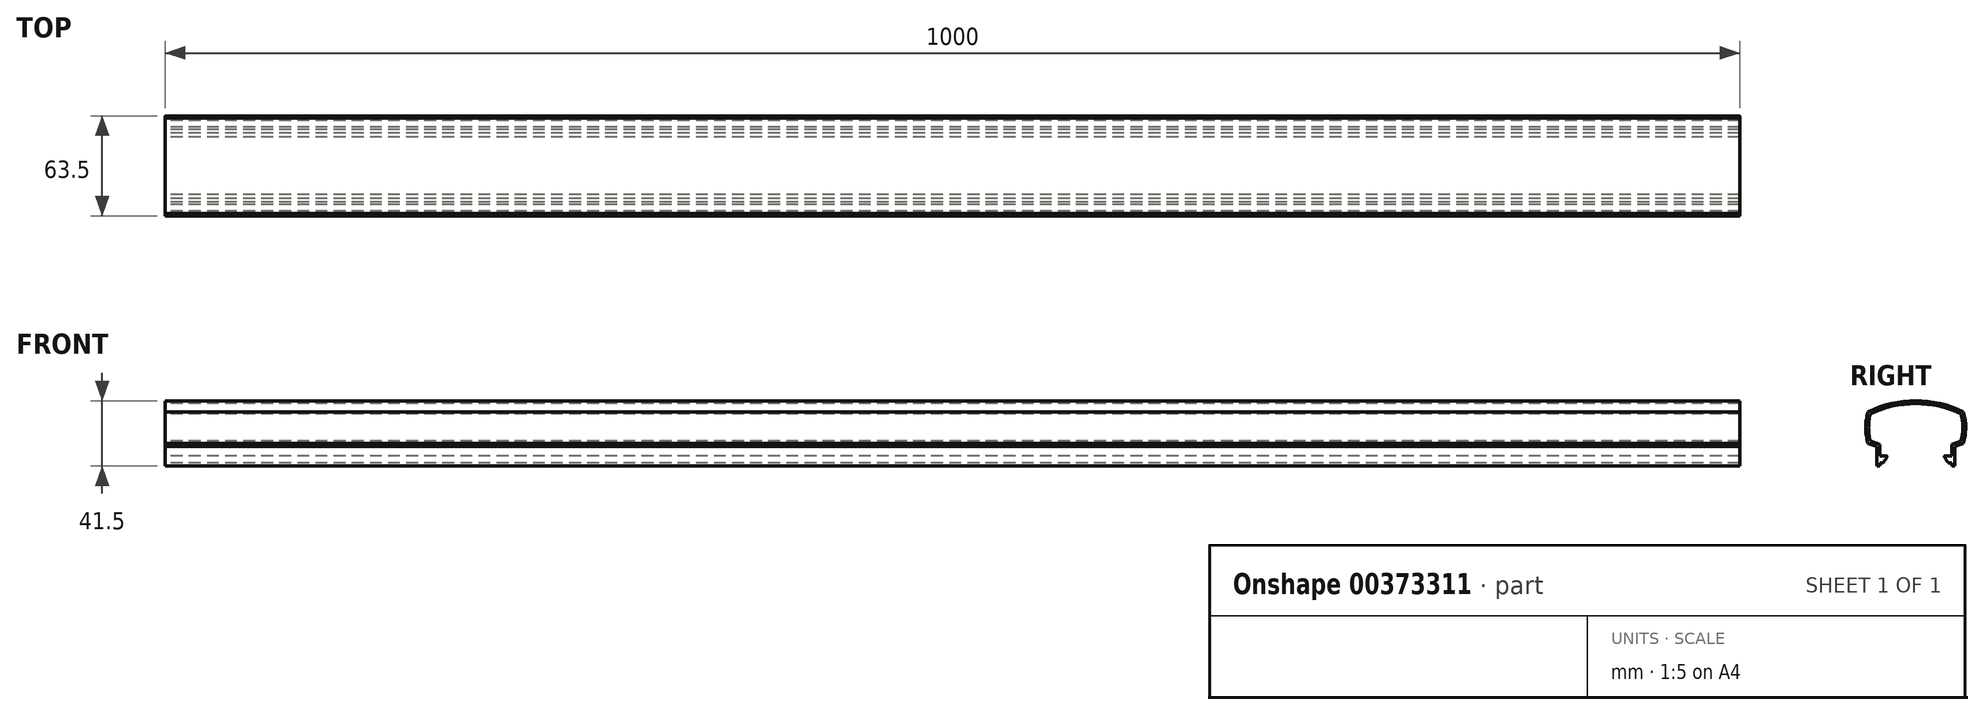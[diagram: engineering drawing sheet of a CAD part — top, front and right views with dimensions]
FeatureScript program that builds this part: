
annotation { "Feature Type Name" : "Feature", "Feature Type Description" : "" }
export const myFeature = defineFeature(function(context is Context, id is Id, definition is map)
    precondition{}
    {
        {
            var Q0;
            Q0=qCreatedBy(makeId("Right.planeOp"),FACE);
            var sketch = newSketch(context, id + "F0", { "sketchPlane" : qUnion([Q0])});
            skLineSegment(sketch, "E0.MirrorCS", {"start": v(56.45, 12.5) * mm, "end": v(56.45, 0) * mm});
            skLineSegment(sketch, "E1.MirrorCS", {"start": v(7.05, 12.5) * mm, "end": v(7.05, 0) * mm});
            skLineSegment(sketch, "E2", {"start": v(56.45, 12.5) * mm, "end": v(62.05, 14.54) * mm});
            skArc(sketch, "E3.trimOffspring", {"start": v(62.05, 14.54) * mm, "mid": v(63.5, 24.45) * mm, "end": v(62.08, 34.36) * mm});
            skArc(sketch, "E4", {"start": v(62.08, 34.36) * mm, "mid": v(31.75, 41.5) * mm, "end": v(1.42, 34.36) * mm});
            skArc(sketch, "E5.MirrorCS", {"start": v(1.45, 14.54) * mm, "mid": v(0, 24.45) * mm, "end": v(1.42, 34.36) * mm});
            skLineSegment(sketch, "E6.MirrorCS", {"start": v(7.05, 12.5) * mm, "end": v(1.45, 14.54) * mm});
            skLineSegment(sketch, "E7.0", {"start": v(8.85, 13.76) * mm, "end": v(8.85, 6.6) * mm});
            skLineSegment(sketch, "E7.1", {"start": v(8.85, 13.76) * mm, "end": v(2.93, 15.92) * mm});
            skArc(sketch, "E7.2", {"start": v(2.93, 15.92) * mm, "mid": v(1.8, 24.5) * mm, "end": v(2.93, 33.1) * mm});
            skLineSegment(sketch, "E7.3", {"start": v(54.65, 13.76) * mm, "end": v(54.65, 6.6) * mm});
            skLineSegment(sketch, "E7.4", {"start": v(54.65, 13.76) * mm, "end": v(60.57, 15.92) * mm});
            skArc(sketch, "E7.5", {"start": v(60.57, 15.92) * mm, "mid": v(61.7, 24.5) * mm, "end": v(60.57, 33.1) * mm});
            skArc(sketch, "E7.6", {"start": v(60.57, 33.1) * mm, "mid": v(31.75, 39.7) * mm, "end": v(2.93, 33.1) * mm});
            skLineSegment(sketch, "E8", {"start": v(8.85, 2) * mm, "end": v(10.92, 2) * mm});
            skArc(sketch, "E9", {"start": v(13.5, 5.87) * mm, "mid": v(13.48, 6.36) * mm, "end": v(13.05, 6.6) * mm});
            skPoint(sketch, "E10.third.point", {"position": v(-23.76, 19.7) * mm});
            skLineSegment(sketch, "E11", {"start": v(13.05, 6.6) * mm, "end": v(8.85, 6.6) * mm});
            skArc(sketch, "E12.trimOffspring", {"start": v(10.92, 2) * mm, "mid": v(12.32, 3.86) * mm, "end": v(13.5, 5.87) * mm});
            skLineSegment(sketch, "E13.trimOffspring", {"start": v(8.85, 2) * mm, "end": v(8.85, 0) * mm});
            skLineSegment(sketch, "E14.MirrorCS", {"start": v(50.45, 6.6) * mm, "end": v(54.65, 6.6) * mm});
            skArc(sketch, "E15.MirrorCS", {"start": v(50, 5.87) * mm, "mid": v(50.02, 6.36) * mm, "end": v(50.45, 6.6) * mm});
            skArc(sketch, "E16.MirrorCS", {"start": v(52.58, 2) * mm, "mid": v(51.18, 3.86) * mm, "end": v(50, 5.87) * mm});
            skLineSegment(sketch, "E17.MirrorCS", {"start": v(54.65, 2) * mm, "end": v(52.58, 2) * mm});
            skLineSegment(sketch, "E18.trimOffspring", {"start": v(54.65, 2) * mm, "end": v(54.65, 0) * mm});
            skLineSegment(sketch, "E19", {"start": v(7.05, 0) * mm, "end": v(8.85, 0) * mm});
            skLineSegment(sketch, "E20", {"start": v(54.65, 0) * mm, "end": v(56.45, 0) * mm});
            skSolve(sketch);
        }
        {
            var Q0;
            Q0=makeQuery(id+"F0.imprint","IMPRINT",FACE,{"disambiguationData":[TD([[makeQuery(id+"F0.imprint","IMPRINT",EDGE,{"derivedFrom":sQuery(id+"F0.wireOp",EDGE,"E0.MirrorCS")}),-1.0]])]});
            extrude(context, id + "F1", {"entities" : qUnion([Q0]), "depth" : 1000 * mm});
        }
    });
